# Revit family: 634-00-001 DN400
name_source: partatom
category: Pipe Accessories
units: mm (PartAtom-declared; Revit-internal decimal feet)

## family parameters
Always vertical = Yes
Cut with Voids When Loaded = No
Part Type = Valve - Breaks Into
Round Connector Dimension = Use Diameter
Shared = No
Work Plane-Based = No

## types (2) — shared parameters
10 = 10 mm  [stored 0.0328084 ft]
2 = 2 mm  [stored 0.00656168 ft]
Bolt_L = 65 mm  [stored 0.213255 ft]
Bore = 200 mm  [stored 0.656168 ft]
D = 331 mm
D-10 = 321 mm
D1 = 240 mm  [stored 0.787402 ft]
D11 = 274 mm
D12 = 15 mm  [stored 0.0492126 ft]
D1_L = 130 mm  [stored 0.426509 ft]
D2 = 41 mm  [stored 0.134514 ft]
D2_L = 81 mm  [stored 0.265748 ft]
D2_L2 = 105 mm
DN = 400 mm
DN400_PN16_AVK ref. no. 634-442-00-016 = 634-396-00-036
DN400_PN16_AVK ref. no. 634-442-00-036 = 634-356-00-036
Description_ = AVK SUPA MAXI™ END CAP, PN16
FL_T = 28 mm  [stored 0.0918635 ft]
L = 158 mm
L-L1 = 41 mm  [stored 0.134514 ft]
L1 = 79 mm
Nut = 16 mm
Radius = 60 mm  [stored 0.19685 ft]
S1 = 196 mm  [stored 0.643045 ft]
S2 = 221 mm  [stored 0.725066 ft]
Search_table = 634-00-001 DN400
URL product pages = https://www.avkvalves.com
zero-valued in all types: Default Elevation, Thickness

## type names (no varying parameters)
- DN400_PN16_AVK ref. no. 634-442-00-016
- DN400_PN16_AVK ref. no. 634-442-00-036

note: [stored X ft] marks values corroborated as IEEE doubles in the binary element streams (Revit-internal decimal feet)

## geometry (parser evidence)
native form markers: Sweep x4
no freeform markers — native parametric forms only
